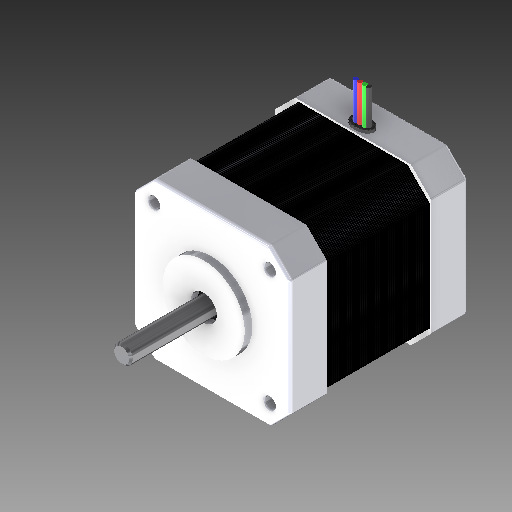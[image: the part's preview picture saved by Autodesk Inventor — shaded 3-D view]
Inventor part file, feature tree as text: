
AUTODESK INVENTOR PART (.ipt)
format: ipt  version: 2019 (Build 230136000, 136)  size: 1,100,800 bytes
history: native  units: mm
features: extrude x12, sketch x4, hole x4, fillet x4, chamfer x2, plane x1, pattern_linear x1, projected_geometry x1
ambient origin geometry x8: Origin, YZ Plane, XZ Plane, XY Plane, X Axis, Y Axis, Z Axis, Center Point
bodies: Solid1 (feature_tree)
feature tree (29):
  sketch  "Sketch1"  dims[d0=7.0mm d1=22.0mm]
  extrude  "Extrusion1"  Depth=22.0mm
  extrude  "Extrusion2"  Depth=31.0mm
  extrude  "Extrusion3"  Depth=3.0mm
  plane  "Work Plane2"
  extrude  "Extrusion7"  Depth=10.0mm
  extrude  "Extrusion8"  Depth=10.0mm
  chamfer  "Chamfer1"  Distance=42.0mm
  pattern_linear  "Rectangular Pattern2"  Spacing1=42.0mm  [1 undecoded]
  hole  "Hole1"  [1 undecoded]
  hole  "Hole2"  [1 undecoded]
  hole  "Hole3"  [1 undecoded]
  hole  "Hole4"  [1 undecoded]
  extrude  "Extrusion9"  Depth=10.0mm
  fillet  "Fillet1"  Radius=24.0mm
  fillet  "Fillet2"  Radius=2.0mm
  chamfer  "Chamfer2"  Distance=48.0mm
  fillet  "Fillet3"  [1 undecoded]
  sketch  "Sketch6"  dims[d10=3.0mm d11=3.0mm d12=3.0mm d39=42.0mm d40=42.0mm d41=135.0deg d42=51.618795mm d43=51.618795mm d44=25.809398mm d45=25.809398mm d46=24.0mm d47=0.0mm d48=2.0mm d49=0.0mm d50=48.0mm d51=0.0mm d60=-10.0mm d126=28.0mm d127=0.0mm d128=1.0mm d129=1.0mm d130=1.0mm d131=1.0mm d132=0.5mm d134=0.5mm d135=0.5mm d136=0.5mm d137=0.5mm d138=1.0mm d139=1.0mm d140=0.5mm d141=0.0mm d145=0.125mm d146=2.0mm d147=45.0deg d148=560.0mm d150=0.5mm d151=10.0mm d152=10.0mm d153=6.0mm d154=6.0mm d155=4.0mm d156=2.0mm d157=90.0deg d158=3.0mm d159=0.0mm d160=10.0mm d161=10.0mm d162=6.0mm d163=6.0mm d164=4.0mm d165=2.0mm d166=90.0deg d167=3.0mm d168=0.0mm d169=10.0mm d170=10.0mm d171=6.0mm d172=6.0mm d173=4.0mm d174=2.0mm d175=90.0deg d176=3.0mm d177=0.0mm d178=10.0mm d179=10.0mm d180=6.0mm d181=6.0mm d182=4.0mm d183=2.0mm d184=90.0deg d185=3.0mm d186=0.0mm d187=48.0mm d188=0.0mm d189=47.0mm d190=0.0mm d191=1.0mm d192=1.0mm d193=0.5mm d194=2.0mm d195=45.0deg d196=0.5mm d197=1.2mm d198=40.0mm d200=1.2mm d201=10.0mm d203=10.0mm d205=2.5mm d206=2.5mm d207=1.0mm d208=0.0mm d209=0.3mm d210=10.0mm d211=0.0mm d212=10.0mm d213=0.0mm d214=10.0mm d215=0.0mm d216=10.0mm d217=0.0mm d218=0.2mm d219=5.0mm d220=0.0mm d221=0.0mm]
  extrude  "Extrusion10"  Depth=10.0mm TaperAngle=0.0deg
  fillet  "Fillet4"  Radius=1.0mm
  extrude  "Extrusion11"  Depth=10.0mm
  extrude  "Extrusion12"  Depth=10.0mm
  extrude  "Extrusion13"  Depth=10.0mm
  extrude  "Extrusion14"  Depth=10.0mm
  extrude  "Extrusion15"  Depth=10.0mm
  sketch  "Sketch4"  dims[d4=5.0mm d5=31.0mm]
  projected_geometry  "Projected Loop2"
  sketch  "Sketch5"  dims[d6=31.0mm d9=3.0mm]
note: 6 required parameter values undecoded (feature->parameter linkage not recoverable at this tier; creation-order binding heuristic only, values carry confidence <= 0.55)
